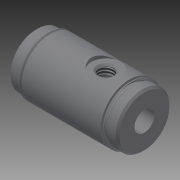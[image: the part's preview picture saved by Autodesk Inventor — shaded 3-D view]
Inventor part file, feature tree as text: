
AUTODESK INVENTOR PART (.ipt)
format: ipt  version: 2014 (Build 180170000, 170)  size: 206,848 bytes
history: native  units: in
note: dims shown in document units (in); Inventor stores cm internally (conversion verified against a paired STEP export)
features: other x49, sketch x5, revolve x4, hole x1, thread x1
ambient origin geometry x8: Origin, YZ Plane, XZ Plane, XY Plane, X Axis, Y Axis, Z Axis, Center Point
bodies: Solid1 (feature_tree)
feature tree (60):
  revolve  "Revolution1"  Angle=360.0deg
  hole  "Hole1"  [1 undecoded]
  revolve  "Revolution2"  [1 undecoded]
  thread  "Thread1"  [1 undecoded]
  revolve  "Revolution3"  [1 undecoded]
  revolve  "Revolution4"  [1 undecoded]
  other  "ba2_XY"
  other  "ba2_YZ"
  other  "ba2_ZX"
  other  "ba2_X"
  other  "ba2_Y"
  other  "ba2_Z"
  other  "ba2_Center"
  other  "centar_XY"
  other  "centar_YZ"
  other  "centar_ZX"
  other  "centar_X"
  other  "centar_Y"
  other  "centar_Z"
  other  "centar_Center"
  other  "d1_XY"
  other  "d1_YZ"
  other  "d1_ZX"
  other  "d1_X"
  other  "d1_Y"
  other  "d1_Z"
  other  "d1_Center"
  other  "d2_XY"
  other  "d2_YZ"
  other  "d2_ZX"
  other  "d2_X"
  other  "d2_Y"
  other  "d2_Z"
  other  "d2_Center"
  other  "to_cyl_A_XY"
  other  "to_cyl_A_YZ"
  other  "to_cyl_A_ZX"
  other  "to_cyl_A_X"
  other  "to_cyl_A_Y"
  other  "to_cyl_A_Z"
  other  "to_cyl_A_Center"
  other  "to_cyl_B_XY"
  other  "to_cyl_B_YZ"
  other  "to_cyl_B_ZX"
  other  "to_cyl_B_X"
  other  "to_cyl_B_Y"
  other  "to_cyl_B_Z"
  other  "to_cyl_B_Center"
  other  "to_rod_A_XY"
  other  "to_rod_A_YZ"
  other  "to_rod_A_ZX"
  other  "to_rod_A_X"
  other  "to_rod_A_Y"
  other  "to_rod_A_Z"
  other  "to_rod_A_Center"
  sketch  "Sketch_1"  dims[d0=360.0deg]
  sketch  "Sketch2"  dims[d1=0.21in d2=0.75in d3=0.375in d4=0.25in d5=0.5635in d6=1.156in d7=0.0in d8=360.0deg]
  sketch  "Sketch_6"  dims[d9=0.0955in d10=0.1018in d11=360.0deg]
  sketch  "Sketch_8"  dims[d12=360.0deg]
  sketch  "Sketch_14"
note: 5 required parameter values undecoded (feature->parameter linkage not recoverable at this tier; creation-order binding heuristic only, values carry confidence <= 0.55)
